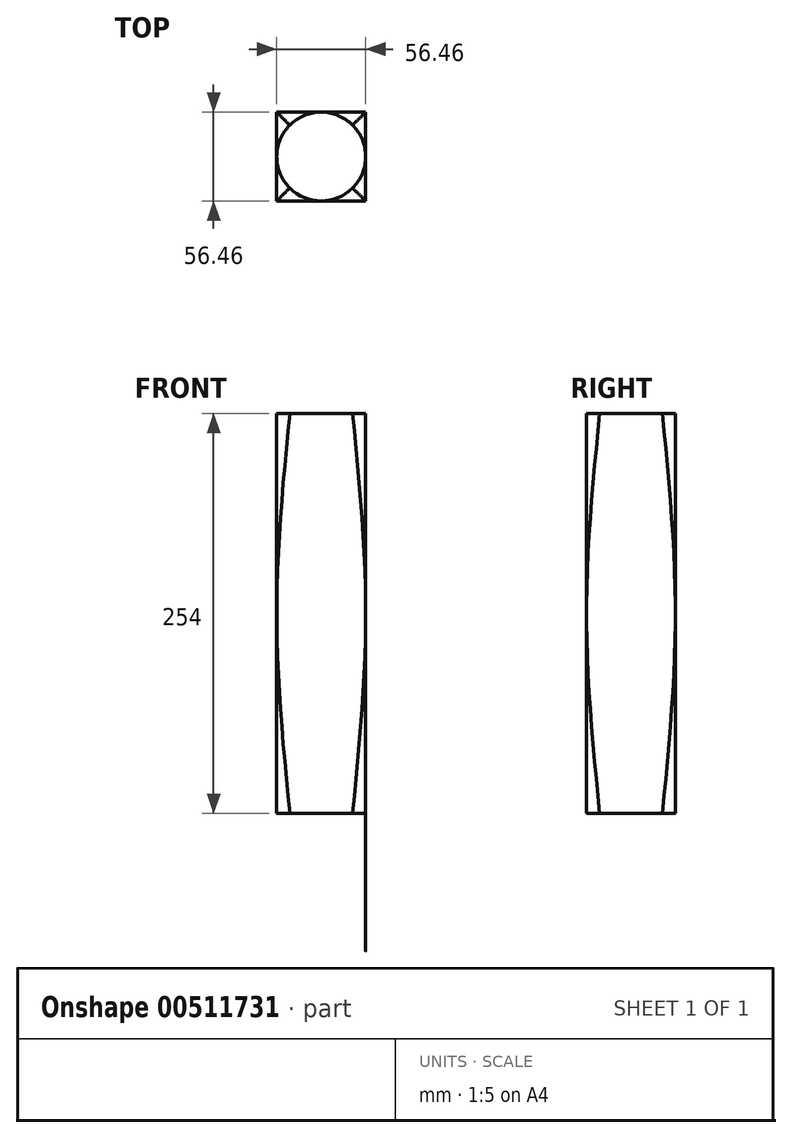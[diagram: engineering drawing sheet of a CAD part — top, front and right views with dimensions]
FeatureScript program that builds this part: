
annotation { "Feature Type Name" : "Feature", "Feature Type Description" : "" }
export const myFeature = defineFeature(function(context is Context, id is Id, definition is map)
    precondition{}
    {
        {
            var Q0;
            Q0=qCreatedBy(makeId("Top.planeOp"),FACE);
            var sketch = newSketch(context, id + "F0", { "sketchPlane" : qUnion([Q0])});
            skCircle(sketch, "E0", {"center": v(0, 0) * mm, "radius": 28.23 * mm});
            skSolve(sketch);
        }
        {
            var Q0;
            Q0=qCreatedBy(makeId("Top.planeOp"),FACE);
            cPlane(context, id + "F1", {"entities" : qUnion([Q0]), "cplaneType" : CPlaneType.OFFSET, "offset" : 127 * mm, "width" : 152.4 * mm, "height" : 152.4 * mm});
        }
        {
            var Q0;
            Q0=qCreatedBy(id+"F1.planeOp",FACE);
            var sketch = newSketch(context, id + "F2", { "sketchPlane" : qUnion([Q0])});
            skLineSegment(sketch, "E1.bottom", {"start": v(28.23, 28.23) * mm, "end": v(-28.23, 28.23) * mm});
            skLineSegment(sketch, "E1.top", {"start": v(28.23, -28.23) * mm, "end": v(-28.23, -28.23) * mm});
            skLineSegment(sketch, "E1.left", {"start": v(28.23, 28.23) * mm, "end": v(28.23, -28.23) * mm});
            skLineSegment(sketch, "E1.right", {"start": v(-28.23, 28.23) * mm, "end": v(-28.23, -28.23) * mm});
            skPoint(sketch, "E1.middle", {"position": v(0, 0) * mm});
            skSolve(sketch);
        }
        {
            var Q0;
            Q0=qCreatedBy(id+"F1.planeOp",FACE);
            cPlane(context, id + "F3", {"entities" : qUnion([Q0]), "cplaneType" : CPlaneType.OFFSET, "offset" : 127 * mm, "width" : 152.4 * mm, "height" : 152.4 * mm});
        }
        {
            var Q0;
            Q0=qCreatedBy(id+"F3.planeOp",FACE);
            var sketch = newSketch(context, id + "F4", { "sketchPlane" : qUnion([Q0])});
            skCircle(sketch, "E2", {"center": v(0, 0) * mm, "radius": 28.23 * mm});
            skSolve(sketch);
        }
        {
            var Q0;
            Q0=makeQuery(id+"F4.imprint","IMPRINT",FACE,{"disambiguationData":[TD([[makeQuery(id+"F4.imprint","IMPRINT",EDGE,{"derivedFrom":sQuery(id+"F4.wireOp",EDGE,"E2")}),1.0]])]});
            var Q1;
            Q1=makeQuery(id+"F2.imprint","IMPRINT",FACE,{"disambiguationData":[TD([[makeQuery(id+"F2.imprint","IMPRINT",EDGE,{"derivedFrom":sQuery(id+"F2.wireOp",EDGE,"E1.bottom")}),1.0]])]});
            var Q2;
            Q2=makeQuery(id+"F0.imprint","IMPRINT",FACE,{"disambiguationData":[TD([[makeQuery(id+"F0.imprint","IMPRINT",EDGE,{"derivedFrom":sQuery(id+"F0.wireOp",EDGE,"E0")}),1.0]])]});
            loft(context, id + "F5", {"sheetProfilesArray" : [{ "sheetProfileEntities" : qUnion([Q0]) }, { "sheetProfileEntities" : qUnion([Q1]) }, { "sheetProfileEntities" : qUnion([Q2]) }]});
        }
    });
